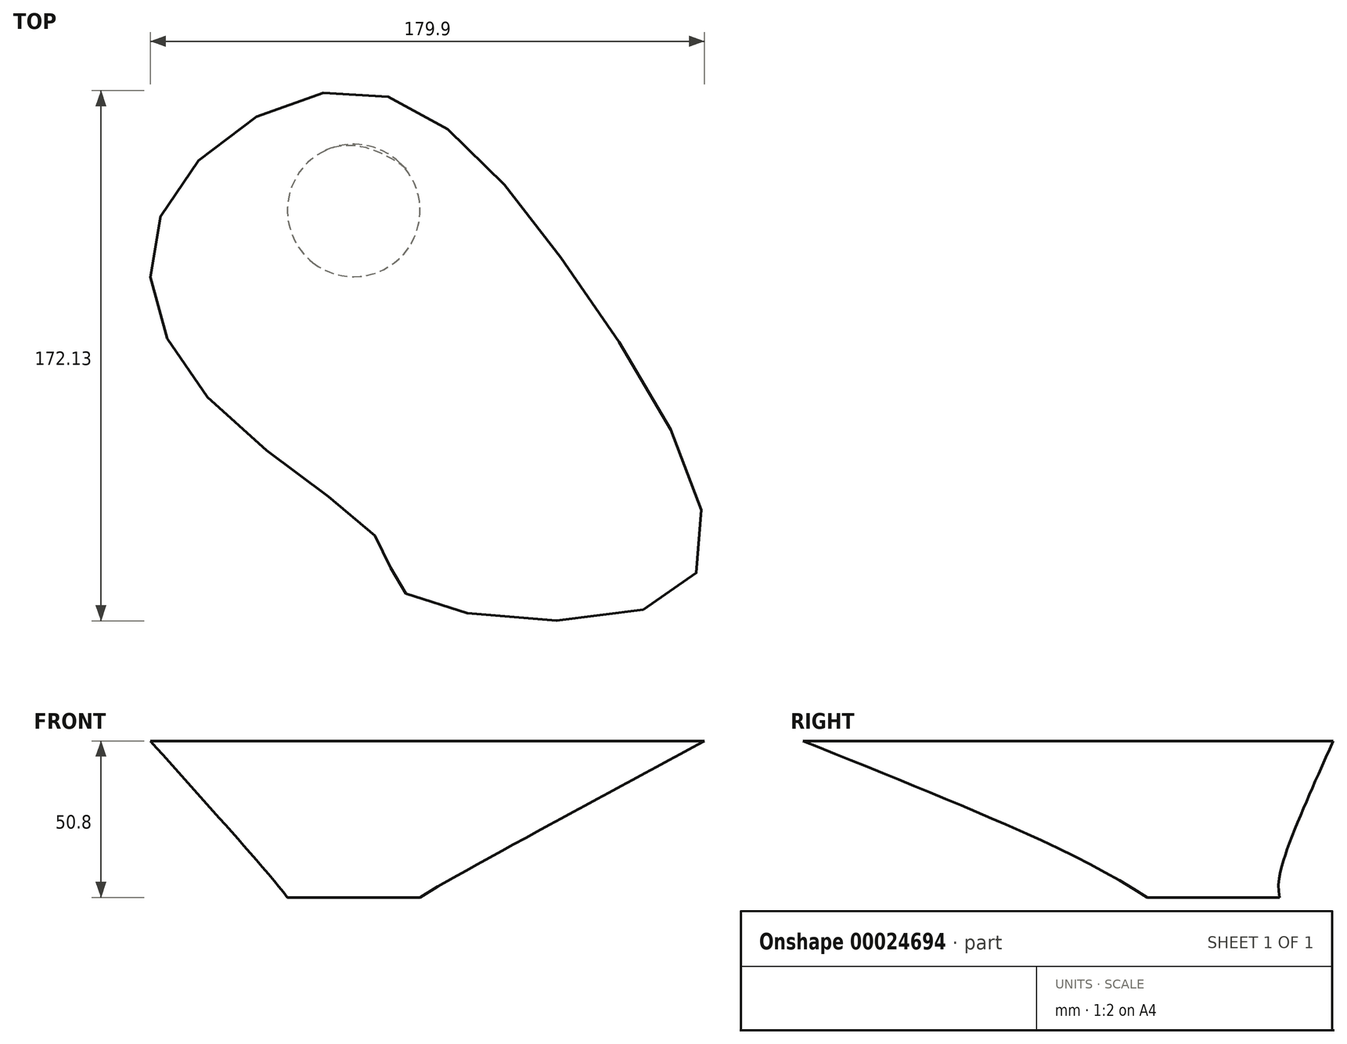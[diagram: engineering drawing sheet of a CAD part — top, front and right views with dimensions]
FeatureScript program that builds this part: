
annotation { "Feature Type Name" : "Feature", "Feature Type Description" : "" }
export const myFeature = defineFeature(function(context is Context, id is Id, definition is map)
    precondition{}
    {
        {
            var Q0;
            Q0=qCreatedBy(makeId("Top.planeOp"),FACE);
            var sketch = newSketch(context, id + "F0", { "sketchPlane" : qUnion([Q0])});
            skCircle(sketch, "E0", {"center": v(0, 0) * mm, "radius": 21.52 * mm});
            skSolve(sketch);
        }
        {
            var Q0;
            Q0=qCreatedBy(makeId("Top.planeOp"),FACE);
            cPlane(context, id + "F1", {"entities" : qUnion([Q0]), "cplaneType" : CPlaneType.OFFSET, "offset" : 50.8 * mm, "width" : 152.4 * mm, "height" : 152.4 * mm});
        }
        {
            var Q0;
            Q0=qCreatedBy(id+"F1.planeOp",FACE);
            var sketch = newSketch(context, id + "F2", { "sketchPlane" : qUnion([Q0])});
            skFitSpline(sketch, "E1", {"points": [v(-47.4, -60.64) * mm, v(-61.87, 0) * mm, v(0, 38.88) * mm, v(72.67, -22.97) * mm, v(107.41, -122.56) * mm, v(16.17, -123.81) * mm, v(10.35, -110.37) * mm, v(-47.4, -60.64) * mm]});
            skSolve(sketch);
        }
        {
            var Q0;
            Q0=makeQuery(id+"F2.imprint","IMPRINT",FACE,{"disambiguationData":[TD([[makeQuery(id+"F2.imprint","IMPRINT",EDGE,{"derivedFrom":sQuery(id+"F2.wireOp",EDGE,"E1")}),-1.0]])]});
            var Q1;
            Q1=makeQuery(id+"F0.imprint","IMPRINT",FACE,{"disambiguationData":[TD([[makeQuery(id+"F0.imprint","IMPRINT",EDGE,{"derivedFrom":sQuery(id+"F0.wireOp",EDGE,"E0")}),1.0]])]});
            loft(context, id + "F3", {"sheetProfilesArray" : [{ "sheetProfileEntities" : qUnion([Q0]) }, { "sheetProfileEntities" : qUnion([Q1]) }]});
        }
    });
